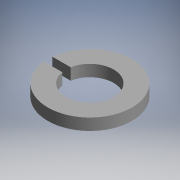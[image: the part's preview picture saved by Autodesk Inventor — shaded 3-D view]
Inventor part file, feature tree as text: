
AUTODESK INVENTOR PART (.ipt)
format: ipt  version: 2017.3 (Build 213256000, 256)  size: 97,792 bytes
history: native  units: mm (DEFAULTED — no unit token found)
features: other x14, extrude x1, sketch x1
ambient origin geometry x8: Origin, YZ Plane, XZ Plane, XY Plane, X Axis, Y Axis, Z Axis, Center Point
bodies: Solid1 (feature_tree)
feature tree (16):
  extrude  "Extrusion1"  TaperAngle=0.0deg  [1 undecoded]
  other  "spring_washer_to_bolt_XY"
  other  "spring_washer_to_bolt_YZ"
  other  "spring_washer_to_bolt_ZX"
  other  "spring_washer_to_bolt_X"
  other  "spring_washer_to_bolt_Y"
  other  "spring_washer_to_bolt_Z"
  other  "spring_washer_to_bolt_Center"
  other  "spring_washer_to_washer_XY"
  other  "spring_washer_to_washer_YZ"
  other  "spring_washer_to_washer_ZX"
  other  "spring_washer_to_washer_X"
  other  "spring_washer_to_washer_Y"
  other  "spring_washer_to_washer_Z"
  other  "spring_washer_to_washer_Center"
  sketch  "Sketch_1"  dims[d0=2.0mm d1=0.0mm d2=0.0mm d3=0.0mm]
note: 1 required parameter value undecoded (feature->parameter linkage not recoverable at this tier; creation-order binding heuristic only, values carry confidence <= 0.55)
